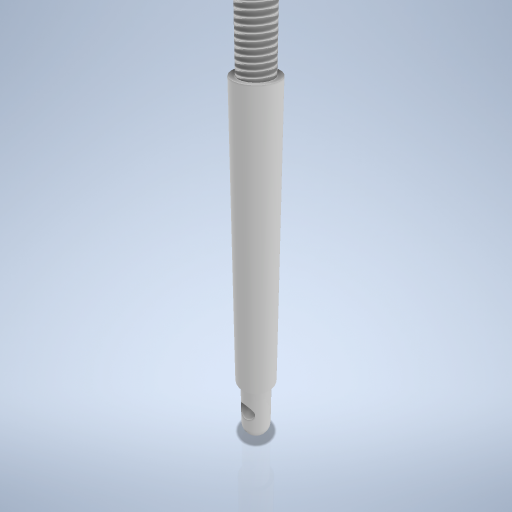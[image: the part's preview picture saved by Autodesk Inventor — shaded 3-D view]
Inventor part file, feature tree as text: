
AUTODESK INVENTOR PART (.ipt)
format: ipt  version: 2024.2 (Build 282272000, 272)  size: 271,872 bytes
history: native  units: mm
features: sketch x2, revolve x1, thread x1, plane x1, hole x1
ambient origin geometry x8: Origin, YZ Plane, XZ Plane, XY Plane, X Axis, Y Axis, Z Axis, Center Point
bodies: Volumenkörper1 (feature_tree)
feature tree (6):
  revolve  "Umdrehung1"
  thread  "Gewinde1"  [1 undecoded]
  plane  "Arbeitsebene1"
  hole  "Bohrung1"  [1 undecoded]
  sketch  "Skizze1"  dims[d1=3.0mm d2=4.0mm]
  sketch  "Skizze2"  dims[d5=30.0mm d6=0.5mm d7=6.0mm d9=90.0deg d10=18.0mm d11=0.0mm d12=1.75mm d13=3.5mm d14=2.0mm d15=6.0mm d16=4.0mm d17=2.0mm d18=90.0deg d19=8.0mm d20=0.0mm]
note: 2 required parameter values undecoded (feature->parameter linkage not recoverable at this tier; creation-order binding heuristic only, values carry confidence <= 0.55)
